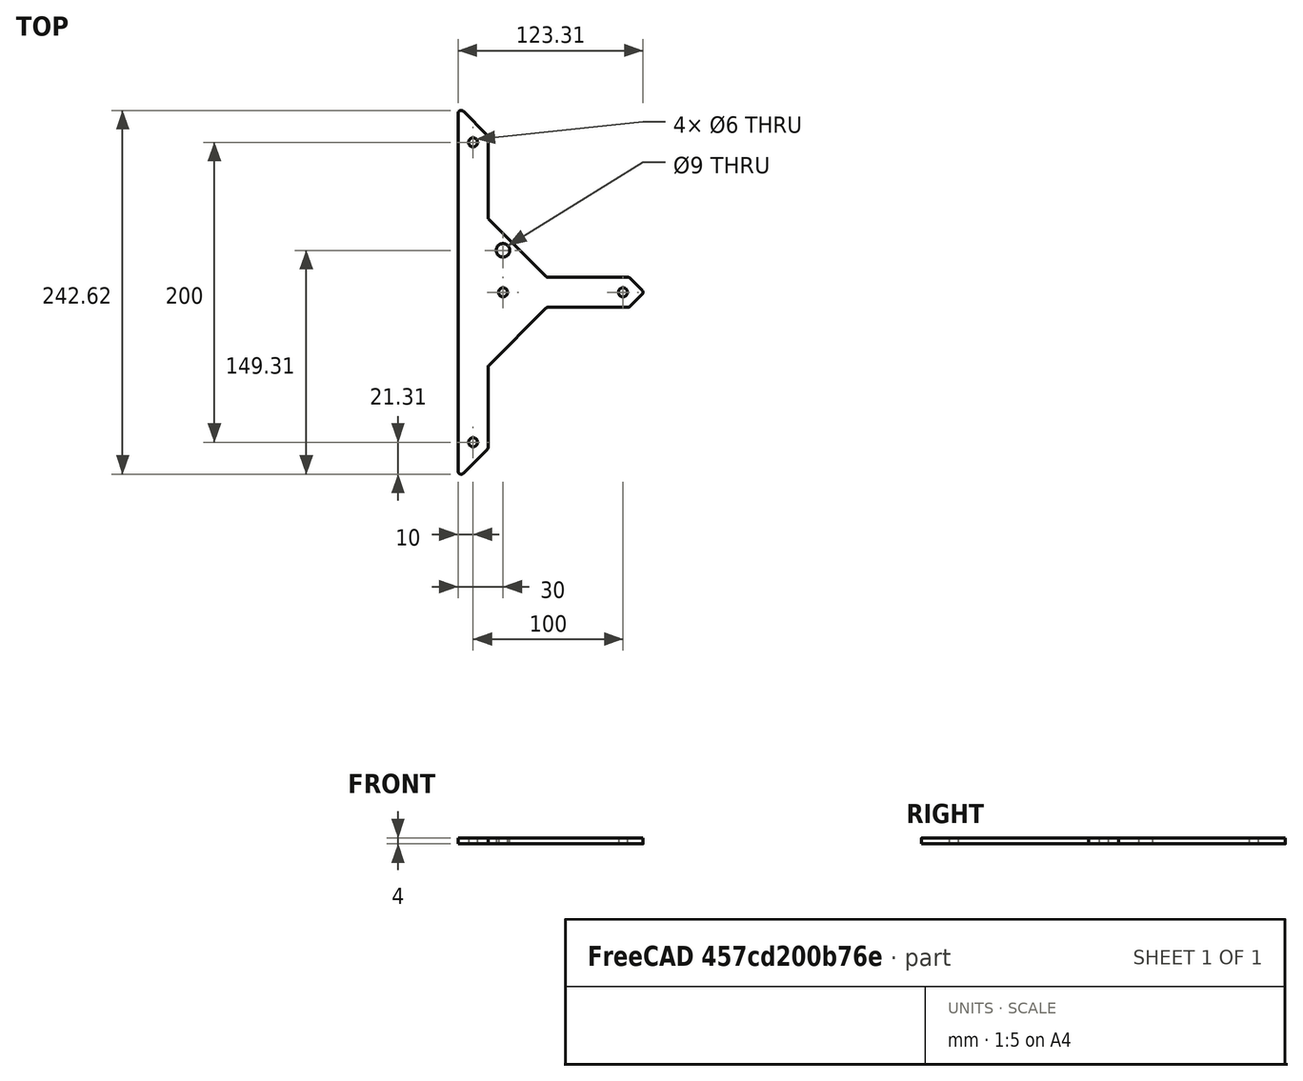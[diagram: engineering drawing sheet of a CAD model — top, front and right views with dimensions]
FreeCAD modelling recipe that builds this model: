
FCSTD DOCUMENT  (FreeCAD 0.19R24267 +99 (Git))
Label: V2 Enclosure middle T bracket
License: All rights reserved
LicenseURL: http://en.wikipedia.org/wiki/All_rights_reserved
objects: Sketcher::SketchObject×1, PartDesign::Pad×1, PartDesign::Body×1
note: 4 computed .brp shape members not serialized (recipe doc carries the construction recipe); baked Part::Feature solids carry a one-line shape summary decoded from their .brp

FEATURE [Sketcher::SketchObject] Sketch
  FullyConstrained = true
  MapMode = 5
  Support = -> [XY_Plane]
  sketch-geometry (33):
    g0: LineSegment StartX=10 StartY=0 StartZ=0 EndX=10 EndY=-114.142 EndZ=0
    g1: Circle CenterX=10 CenterY=-100 CenterZ=0 NormalX=0 NormalY=0 NormalZ=1 AngleXU=0 Radius=3
    g2: LineSegment StartX=0 StartY=119.314 StartZ=0 EndX=0 EndY=-119.314 EndZ=0
    g3: LineSegment StartX=20 StartY=-50 StartZ=0 EndX=20 EndY=-103.314 EndZ=0
    g4: LineSegment StartX=20.5858 StartY=-48.5858 StartZ=0 EndX=58.5858 EndY=-10.5858 EndZ=0
    g5: LineSegment StartX=60 StartY=-10 StartZ=0 EndX=113.314 EndY=-10 EndZ=0
    g6: LineSegment StartX=113.314 StartY=10 StartZ=0 EndX=60 EndY=10 EndZ=0
    g7: LineSegment StartX=3.41421 StartY=-120.728 StartZ=0 EndX=19.4142 EndY=-104.728 EndZ=0
    g8: ArcOfCircle CenterX=2 CenterY=-119.314 CenterZ=0 NormalX=0 NormalY=0 NormalZ=1 AngleXU=0 Radius=2 StartAngle=3.14159 EndAngle=5.49779
    g9: ArcOfCircle CenterX=18 CenterY=-103.314 CenterZ=0 NormalX=0 NormalY=0 NormalZ=1 AngleXU=0 Radius=2 StartAngle=5.49779 EndAngle=6.28319
    g10: ArcOfCircle CenterX=22 CenterY=-50 CenterZ=0 NormalX=0 NormalY=0 NormalZ=1 AngleXU=0 Radius=2 StartAngle=2.35619 EndAngle=3.14159
    g11: ArcOfCircle CenterX=60 CenterY=-12 CenterZ=0 NormalX=0 NormalY=0 NormalZ=1 AngleXU=0 Radius=2 StartAngle=1.5708 EndAngle=2.35619
    g12: LineSegment StartX=58.5858 StartY=10.5858 StartZ=0 EndX=20.5858 EndY=48.5858 EndZ=0
    g13: LineSegment StartX=20 StartY=50 StartZ=0 EndX=20 EndY=103.314 EndZ=0
    g14: LineSegment StartX=3.41421 StartY=120.728 StartZ=0 EndX=19.4142 EndY=104.728 EndZ=0
    g15: ArcOfCircle CenterX=2 CenterY=119.314 CenterZ=0 NormalX=0 NormalY=0 NormalZ=1 AngleXU=0 Radius=2 StartAngle=0.785398 EndAngle=3.14159
    g16: ArcOfCircle CenterX=18 CenterY=103.314 CenterZ=0 NormalX=0 NormalY=0 NormalZ=1 AngleXU=0 Radius=2 StartAngle=-2.7e-15 EndAngle=0.785398
    g17: ArcOfCircle CenterX=22 CenterY=50 CenterZ=0 NormalX=0 NormalY=0 NormalZ=1 AngleXU=0 Radius=2 StartAngle=3.14159 EndAngle=3.92699
    g18: ArcOfCircle CenterX=60 CenterY=12 CenterZ=0 NormalX=0 NormalY=0 NormalZ=1 AngleXU=0 Radius=2 StartAngle=3.92699 EndAngle=4.71239
    g19: Circle CenterX=10 CenterY=100 CenterZ=0 NormalX=0 NormalY=0 NormalZ=1 AngleXU=0 Radius=3
    g20: LineSegment StartX=114.728 StartY=9.41421 StartZ=0 EndX=122.728 EndY=1.41421 EndZ=0
    g21: LineSegment StartX=114.728 StartY=-9.41421 StartZ=0 EndX=122.728 EndY=-1.41421 EndZ=0
    g22: ArcOfCircle CenterX=113.314 CenterY=8 CenterZ=0 NormalX=0 NormalY=0 NormalZ=1 AngleXU=0 Radius=2 StartAngle=0.785398 EndAngle=1.5708
    g23: ArcOfCircle CenterX=113.314 CenterY=-8 CenterZ=0 NormalX=0 NormalY=0 NormalZ=1 AngleXU=0 Radius=2 StartAngle=4.71239 EndAngle=5.49779
    g24: ArcOfCircle CenterX=121.314 CenterY=0 CenterZ=0 NormalX=0 NormalY=0 NormalZ=1 AngleXU=0 Radius=2 StartAngle=5.49779 EndAngle=7.06858
    g25: Circle CenterX=110 CenterY=0 CenterZ=0 NormalX=0 NormalY=0 NormalZ=1 AngleXU=0 Radius=10
    g26: Circle CenterX=110 CenterY=0 CenterZ=0 NormalX=0 NormalY=0 NormalZ=1 AngleXU=0 Radius=3
    g27: Circle CenterX=30 CenterY=0 CenterZ=0 NormalX=0 NormalY=0 NormalZ=1 AngleXU=0 Radius=3
    g28: Circle CenterX=30 CenterY=28 CenterZ=0 NormalX=0 NormalY=0 NormalZ=1 AngleXU=0 Radius=4.5
    g29: LineSegment StartX=20 StartY=50 StartZ=0 EndX=20 EndY=-50 EndZ=0
    g30: GeomPoint X=20 Y=0 Z=0
    g31: Circle CenterX=10 CenterY=-100 CenterZ=0 NormalX=0 NormalY=0 NormalZ=1 AngleXU=0 Radius=10
    g32: Circle CenterX=30 CenterY=28 CenterZ=0 NormalX=0 NormalY=0 NormalZ=1 AngleXU=0 Radius=6.5
  constraints (77):
    c: Vertical(g0)
    c: PointOnObject(g1,g0)
    c: Vertical(g3)
    c: Tangent(g2,g8) = -1.5708
    c: Tangent(g7,g8) = -1.5708
    c: Tangent(g3,g9) = 1.5708
    c: Tangent(g7,g9) = -1.5708
    c: Tangent(g4,g10) = 1.5708
    c: Tangent(g3,g10) = -1.5708
    c: Tangent(g4,g11) = 1.5708
    c: Tangent(g5,g11) = 1.5708
    c: Equal(g10,g11)
    c: Equal(g8,g9)
    c: PointOnObject(g0,g7)
    c: Angle(g7,g2) = 0.785398
    c: DistanceX(g3,g5) = 40
    c: DistanceY(g3,g5) = 40
    c: DistanceX(g2,g3) = 20
    c: Radius(g1) = 3
    c: Radius(g8) = 2
    c: Tangent(g14,g15) = 1.5708
    c: Tangent(g2,g15) = -1.5708
    c: Tangent(g14,g16) = 1.5708
    c: Tangent(g13,g16) = -1.5708
    c: Tangent(g13,g17) = 1.5708
    c: Tangent(g12,g17) = 1.5708
    c: Tangent(g6,g18) = 1.5708
    c: Tangent(g12,g18) = 1.5708
    c: Equal(g15,g16)
    c: Equal(g16,g17)
    c: Equal(g17,g18)
    c: Symmetric(g6,g5,g-1)
    c: Symmetric(g3,g13,g-1)
    c: Symmetric(g2,g2,g-1)
    c: Symmetric(g3,g13,g-1)
    c: Equal(g10,g8)
    c: Symmetric(g19,g1,g-1)
    c: Equal(g1,g19)
    c: Tangent(g6,g22) = -1.5708
    c: Tangent(g20,g22) = 1.5708
    c: Tangent(g5,g23) = -1.5708
    c: Tangent(g21,g23) = -1.5708
    c: Tangent(g20,g24) = 1.5708
    c: Tangent(g21,g24) = -1.5708
    c: Equal(g22,g23)
    c: Equal(g23,g24)
    c: Equal(g24,g8)
    c: Horizontal(g6)
    c: Symmetric(g6,g5,g-1)
    c: Angle(g20,g21) = 1.5708
    c: PointOnObject(g25,g-1)
    c: Tangent(g25,g6)
    c: Tangent(g20,g25)
    c: Coincident(g26,g25)
    c: PointOnObject(g27,g-1)
    c: DistanceY(g1,g0) = 100
    c: Equal(g27,g26)
    c: Equal(g26,g1)
    c: DistanceX(g0,g27) = 20
    c: DistanceX(g0,g26) = 100
    c: Radius(g28) = 4.5
    c: Coincident(g29,g13)
    c: Coincident(g29,g3)
    c: PointOnObject(g30,g29)
    c: PointOnObject(g30,g-1)
    c: PointOnObject(g24,g-1)
    c: DistanceY(g5,g6) = 20
    c: PointOnObject(g-1,g2)
    c: Symmetric(g30,g-1,g0)
    c: Coincident(g31,g1)
    c: Tangent(g31,g2)
    c: Tangent(g7,g31)
    c: DistanceX(g13,g28) = 10
    c: DistanceY(g6,g28) = 18
    c: Coincident(g32,g28)
    c: Radius(g32) = 6.5
    c: Equal(g16,g8)
FEATURE [PartDesign::Pad] Pad
  Direction = (1,1,1)
  Length = 4
  Length2 = 100
  Profile = -> Sketch
  Type = 0
FEATURE [PartDesign::Body] Body
  Group = -> [Sketch,Pad]
  Origin = -> Origin
  Tip = -> Pad
